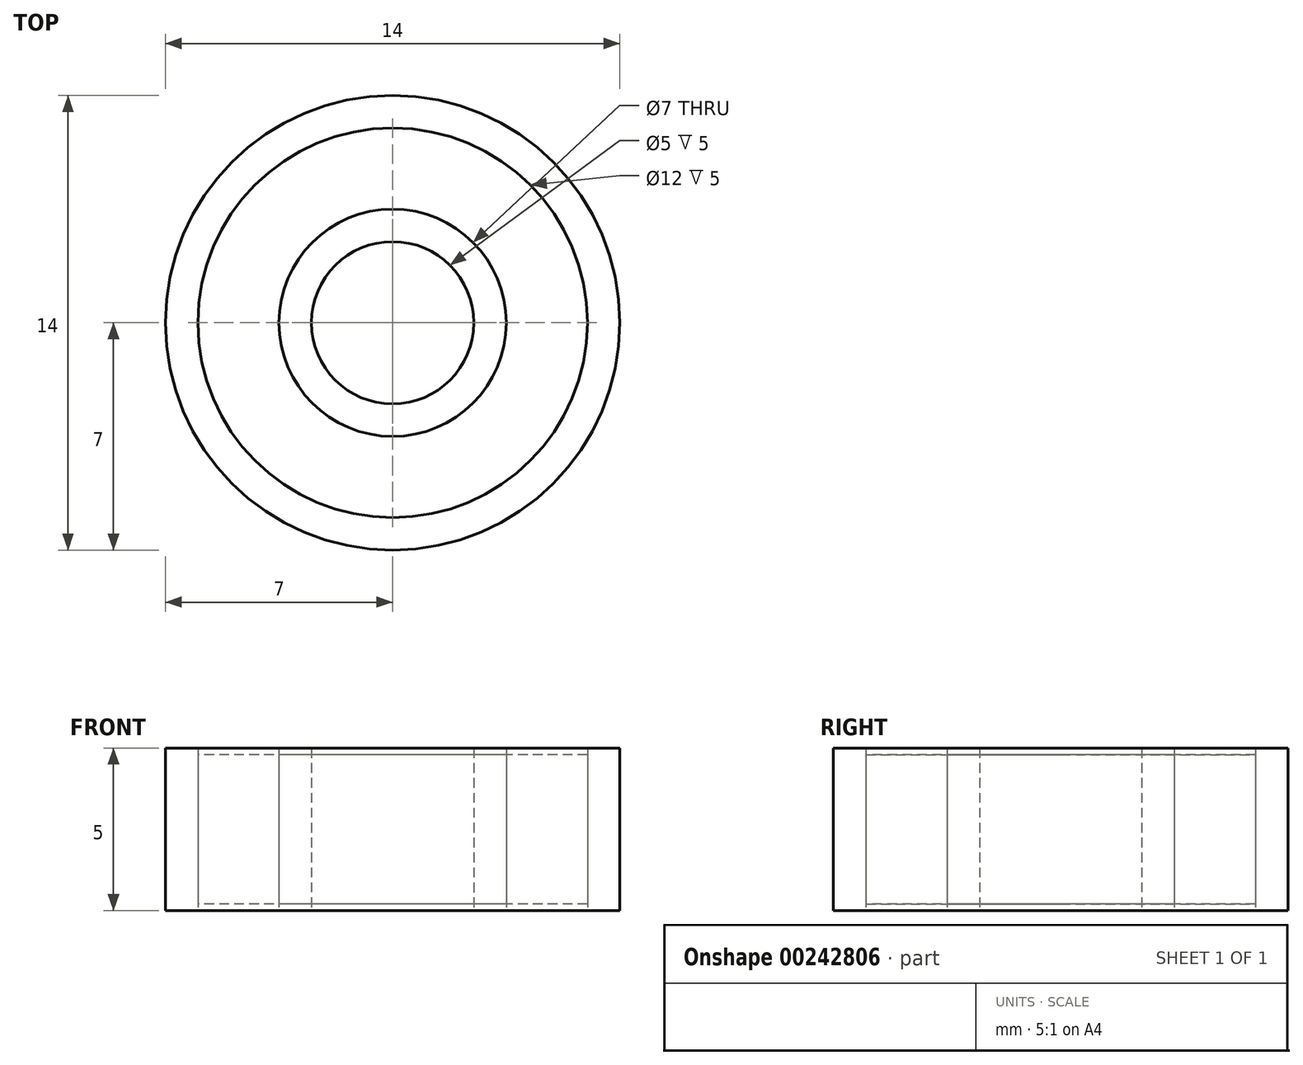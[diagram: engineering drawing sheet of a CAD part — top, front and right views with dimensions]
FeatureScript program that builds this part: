
annotation { "Feature Type Name" : "Feature", "Feature Type Description" : "" }
export const myFeature = defineFeature(function(context is Context, id is Id, definition is map)
    precondition{}
    {
        {
            assignVariable(context, id + "F0", {"name" : "index", "anyValue" : 6});
        }
        {
            assignVariable(context, id + "F1", {"name" : "width", "anyValue" : [6, 7, 7, 5, 5, 6, 5][getVariable(context, 'index')]});
        }
        {
            var Q0;
            Q0=qCreatedBy(makeId("Top.planeOp"),FACE);
            var sketch = newSketch(context, id + "F2", { "sketchPlane" : qUnion([Q0])});
            skCircle(sketch, "E0", {"center": v(0, 0) * mm, "radius": 2.5 * mm});
            skCircle(sketch, "E1", {"center": v(0, 0) * mm, "radius": 3.5 * mm});
            skCircle(sketch, "E2", {"center": v(0, 0) * mm, "radius": 7 * mm});
            skCircle(sketch, "E3", {"center": v(0, 0) * mm, "radius": 6 * mm});
            skSolve(sketch);
        }
        {
            var Q0;
            Q0=qSketchRegion(id+"F2",true);
            var Q1;
            Q1=makeQuery(id+"F2.imprint","IMPRINT",FACE,{"disambiguationData":[TD([[makeQuery(id+"F2.imprint","IMPRINT",EDGE,{"derivedFrom":sQuery(id+"F2.wireOp",EDGE,"E0")}),-1.0]])]});
            extrude(context, id + "F3", {"entities" : qUnion([Q0, Q1]), "endBound" : BoundingType.SYMMETRIC, "depth" : (getVariable(context, 'width')) * mm});
        }
        {
            var Q0;
            Q0=makeQuery(id+"F2.imprint","IMPRINT",FACE,{"disambiguationData":[TD([[makeQuery(id+"F2.imprint","IMPRINT",EDGE,{"derivedFrom":sQuery(id+"F2.wireOp",EDGE,"E1")}),-1.0]])]});
            extrude(context, id + "F4", {"entities" : qUnion([Q0]), "endBound" : BoundingType.SYMMETRIC, "depth" : (getVariable(context, 'width') - 0.4) * mm});
        }
    });
